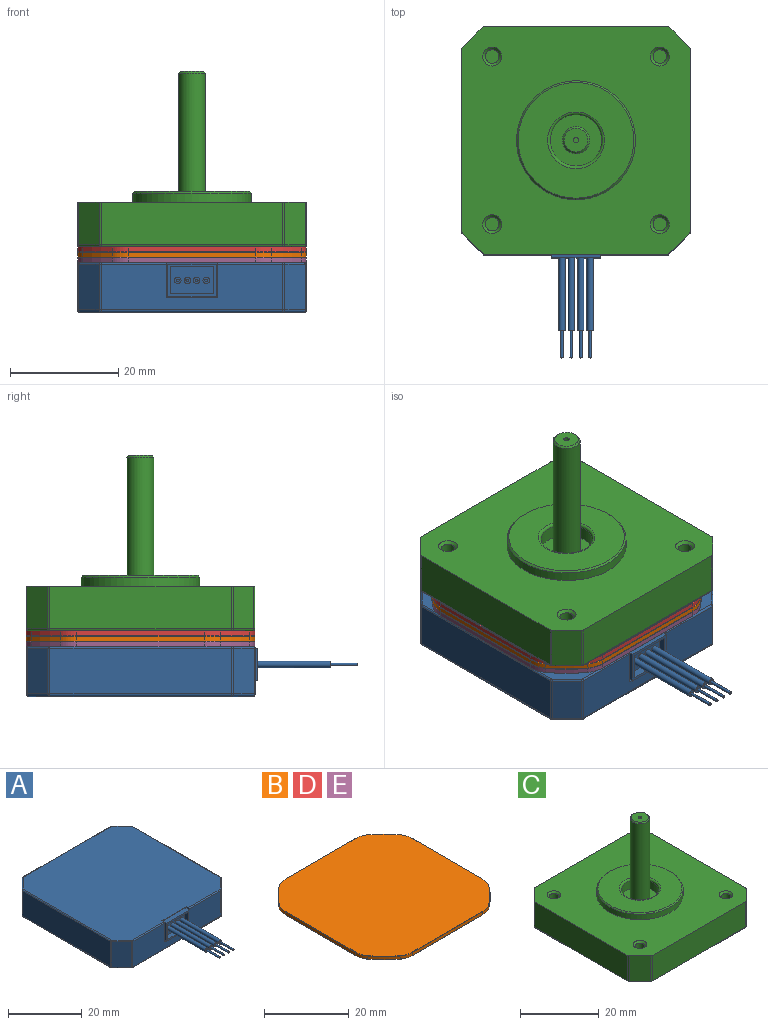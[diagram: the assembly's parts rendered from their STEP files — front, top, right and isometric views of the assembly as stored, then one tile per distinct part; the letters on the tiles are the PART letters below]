
ASSEMBLY  parts=5 mates=2
PART A: 89 faces, bbox 42.3x61.3x9.2 mm
  f0: plane 9.5x6.5mm, normal (0,-1,0), area 7.8mm2, adj f9,f43,f44,f45,f64,f65,f66,f67
  f1: plane 8.4x3.82mm, normal (-0.71,-0.71,0), area 45.4mm2, adj f30,f35,f36,f60
  f2: plane 33.65x8.4mm, normal (0,-1,0), area 223.8mm2, adj f36,f37,f41,f43,f44,f45,f46,f62
  f3: plane 8.4x3.82mm, normal (0.71,-0.71,0), area 45.4mm2, adj f31,f37,f38,f48
  f4: plane 33.65x8.4mm, normal (1,0,0), area 282.7mm2, adj f25,f31,f32,f50
  f5: plane 8.4x3.82mm, normal (0.71,0.71,0), area 45.4mm2, adj f19,f25,f26,f52
  f6: plane 33.65x8.4mm, normal (0,1,0), area 282.7mm2, adj f18,f19,f20,f54
  f7: plane 8.4x3.82mm, normal (-0.71,0.71,0), area 45.4mm2, adj f18,f23,f24,f56
  f8: plane 33.65x8.4mm, normal (-1,0,0), area 282.7mm2, adj f24,f29,f30,f58
  f9: plane 41.7x41.7mm, normal (0,0,1), area 1701.2mm2, adj f0,f43,f45,f46,f47,f48,f49,f50
  f10: plane 41.3x41.3mm, normal (0,0,-1), area 1589.9mm2, adj f20,f23,f26,f29,f32,f35,f38,f41
  f11: cylinder r=4.75mm len=9.5mm, axis (0,0,-1), area 89.5mm2, adj f12,f42
  f12: plane 9.5x9.5mm, normal (0,0,-1), area 51.2mm2, adj f11,f13
  f13: cylinder r=2.5mm len=5mm, axis (0,0,-1), area 3.1mm2, adj f12,f17
  f14: plane 4.4x4.4mm, normal (0,0,-1), area 14.4mm2, adj f15,f17
  f15: cylinder r=0.5mm len=1mm, axis (0,0,-1), area 1.6mm2, adj f14,f16
  f16: plane 1x1mm, normal (0,0,-1), area 0.8mm2, adj f15
  f17: cone r=2.2mm half-angle=45deg, axis (0,0,1), area 6.3mm2, adj f13,f14
  f18: cylinder r=0.5mm len=8.4mm, axis (0,0,-1), area 3.3mm2, adj f6,f7,f21,f55
  f19: cylinder r=0.5mm len=8.4mm, axis (0,0,-1), area 3.3mm2, adj f5,f6,f22,f53
  f20: cylinder r=0.5mm len=33.65mm, axis (-1,0,0), area 26.4mm2, adj f6,f10,f21,f22
  f21: sphere r=0.5mm, area 0.2mm2, adj f18,f20,f23
  f22: sphere r=0.5mm, area 0.2mm2, adj f19,f20,f26
  f23: cylinder r=0.5mm len=4.18mm, axis (-0.71,-0.71,0), area 4.2mm2, adj f7,f10,f21,f27
  f24: cylinder r=0.5mm len=8.4mm, axis (0,0,1), area 3.3mm2, adj f7,f8,f27,f57
  f25: cylinder r=0.5mm len=8.4mm, axis (0,0,-1), area 3.3mm2, adj f4,f5,f28,f51
  f26: cylinder r=0.5mm len=4.18mm, axis (-0.71,0.71,0), area 4.2mm2, adj f5,f10,f22,f28
  f27: sphere r=0.5mm, area 0.2mm2, adj f23,f24,f29
  f28: sphere r=0.5mm, area 0.2mm2, adj f25,f26,f32
  f29: cylinder r=0.5mm len=33.65mm, axis (0,-1,0), area 26.4mm2, adj f8,f10,f27,f33
  f30: cylinder r=0.5mm len=8.4mm, axis (0,0,1), area 3.3mm2, adj f1,f8,f33,f59
  f31: cylinder r=0.5mm len=8.4mm, axis (0,0,-1), area 3.3mm2, adj f3,f4,f34,f49
  f32: cylinder r=0.5mm len=33.65mm, axis (0,1,0), area 26.4mm2, adj f4,f10,f28,f34
  f33: sphere r=0.5mm, area 0.2mm2, adj f29,f30,f35
  f34: sphere r=0.5mm, area 0.2mm2, adj f31,f32,f38
  f35: cylinder r=0.5mm len=4.18mm, axis (0.71,-0.71,0), area 4.2mm2, adj f1,f10,f33,f39
  f36: cylinder r=0.5mm len=8.4mm, axis (0,0,1), area 3.3mm2, adj f1,f2,f39,f61
  f37: cylinder r=0.5mm len=8.4mm, axis (0,0,1), area 3.3mm2, adj f2,f3,f40,f47
  f38: cylinder r=0.5mm len=4.18mm, axis (0.71,0.71,0), area 4.2mm2, adj f3,f10,f34,f40
  f39: sphere r=0.5mm, area 0.2mm2, adj f35,f36,f41
  f40: sphere r=0.5mm, area 0.2mm2, adj f37,f38,f41
  f41: cylinder r=0.5mm len=33.65mm, axis (1,0,0), area 26.4mm2, adj f2,f10,f39,f40
  f42: torus R=5.25mm, axis (0,0,1), area 24.3mm2, adj f10,f11
  f43: plane 6.5x1mm, normal (-1,0,0), area 6.5mm2, adj f0,f2,f9,f44,f46
  f44: plane 9.5x1mm, normal (0,0,1), area 9.5mm2, adj f0,f2,f43,f45
  f45: plane 6.5x1mm, normal (1,0,0), area 6.5mm2, adj f0,f2,f9,f44,f62
  f46: cylinder r=0.3mm len=12.08mm, axis (-1,0,0), area 5.7mm2, adj f2,f9,f43,f47
  f47: torus R=0.2mm, axis (0,0,1), area 0.1mm2, adj f9,f37,f46,f48
  f48: cylinder r=0.3mm len=4.04mm, axis (-0.71,-0.71,0), area 2.5mm2, adj f3,f9,f47,f49
  f49: torus R=0.2mm, axis (0,0,1), area 0.1mm2, adj f9,f31,f48,f50
  f50: cylinder r=0.3mm len=33.65mm, axis (0,-1,0), area 15.9mm2, adj f4,f9,f49,f51
  f51: torus R=0.2mm, axis (0,0,1), area 0.1mm2, adj f9,f25,f50,f52
  f52: cylinder r=0.3mm len=4.04mm, axis (0.71,-0.71,0), area 2.5mm2, adj f5,f9,f51,f53
  f53: torus R=0.2mm, axis (0,0,1), area 0.1mm2, adj f9,f19,f52,f54
  f54: cylinder r=0.3mm len=33.65mm, axis (1,0,0), area 15.9mm2, adj f6,f9,f53,f55
  f55: torus R=0.2mm, axis (0,0,1), area 0.1mm2, adj f9,f18,f54,f56
  f56: cylinder r=0.3mm len=4.04mm, axis (0.71,0.71,0), area 2.5mm2, adj f7,f9,f55,f57
  f57: torus R=0.2mm, axis (0,0,1), area 0.1mm2, adj f9,f24,f56,f58
  f58: cylinder r=0.3mm len=33.65mm, axis (0,1,0), area 15.9mm2, adj f8,f9,f57,f59
  f59: torus R=0.2mm, axis (0,0,1), area 0.1mm2, adj f9,f30,f58,f60
  f60: cylinder r=0.3mm len=4.04mm, axis (-0.71,0.71,0), area 2.5mm2, adj f1,f9,f59,f61
  f61: torus R=0.2mm, axis (0,0,1), area 0.1mm2, adj f9,f36,f60,f62
  f62: cylinder r=0.3mm len=12.08mm, axis (-1,0,0), area 5.7mm2, adj f2,f9,f45,f61
  f63: plane 9x6mm, normal (0,-1,0), area 14mm2, adj f64,f65,f66,f67,f68,f69,f70,f71
  f64: plane 9x1.5mm, normal (0,0,-1), area 13.5mm2, adj f0,f63,f65,f67
  f65: plane 6x1.5mm, normal (1,0,0), area 9mm2, adj f0,f63,f64,f66
  f66: plane 9x1.5mm, normal (0,0,1), area 13.5mm2, adj f0,f63,f65,f67
  f67: plane 6x1.5mm, normal (-1,0,0), area 9mm2, adj f0,f63,f64,f66
  f68: plane 8x1.5mm, normal (0,0,1), area 12mm2, adj f63,f69,f71,f80
  f69: plane 5x1.5mm, normal (-1,0,0), area 7.5mm2, adj f63,f68,f70,f80
  f70: plane 8x1.5mm, normal (0,0,-1), area 12mm2, adj f63,f69,f71,f80
  f71: plane 5x1.5mm, normal (1,0,0), area 7.5mm2, adj f63,f68,f70,f80
  f72: plane 0.5x0.5mm, normal (0,-1,0), area 0.2mm2, adj f74
  f73: plane 0.5x0.5mm, normal (0,-1,0), area 0.2mm2, adj f75
  f74: cylinder r=0.25mm len=5mm, axis (0,1,0), area 7.9mm2, adj f72,f76
  f75: cylinder r=0.25mm len=5mm, axis (0,1,0), area 7.9mm2, adj f73,f77
  f76: plane 1.2x1.2mm, normal (0,-1,0), area 0.9mm2, adj f74,f78
  f77: plane 1.2x1.2mm, normal (0,-1,0), area 0.9mm2, adj f75,f79
  f78: cylinder r=0.6mm len=15mm, axis (0,1,0), area 56.5mm2, adj f76,f80
  f79: cylinder r=0.6mm len=15mm, axis (0,1,0), area 56.5mm2, adj f77,f80
  f80: plane 8x5mm, normal (0,-1,0), area 35.5mm2, adj f68,f69,f70,f71,f78,f79,f82,f86
  f81: plane 1.2x1.2mm, normal (0,-1,0), area 0.9mm2, adj f82,f83
  f82: cylinder r=0.6mm len=15mm, axis (0,1,0), area 56.5mm2, adj f80,f81
  f83: cylinder r=0.25mm len=5mm, axis (0,1,0), area 7.9mm2, adj f81,f84
  f84: plane 0.5x0.5mm, normal (0,-1,0), area 0.2mm2, adj f83
  f85: plane 1.2x1.2mm, normal (0,-1,0), area 0.9mm2, adj f86,f87
  f86: cylinder r=0.6mm len=15mm, axis (0,1,0), area 56.5mm2, adj f80,f85
  f87: cylinder r=0.25mm len=5mm, axis (0,1,0), area 7.9mm2, adj f85,f88
  f88: plane 0.5x0.5mm, normal (0,-1,0), area 0.2mm2, adj f87
PART B: 50 faces, bbox 42.3x42.3x1 mm
  f0: cylinder r=5mm len=2.95mm, axis (0,0,-1), area 2.8mm2, adj f1,f15,f27,f43
  f1: plane 23.59x0.9mm, normal (0,1,0), area 21.2mm2, adj f0,f2,f29,f45
  f2: cylinder r=5mm len=2.95mm, axis (0,0,-1), area 2.8mm2, adj f1,f3,f31,f47
  f3: cylinder r=25mm len=5.44mm, axis (0,0,-1), area 7mm2, adj f2,f4,f33,f49
  f4: cylinder r=5mm len=2.95mm, axis (0,0,-1), area 2.8mm2, adj f3,f5,f32,f48
  f5: plane 23.59x0.9mm, normal (-1,0,0), area 21.2mm2, adj f4,f6,f30,f46
  f6: cylinder r=5mm len=2.95mm, axis (0,0,-1), area 2.8mm2, adj f5,f7,f28,f44
  f7: cylinder r=25mm len=5.44mm, axis (0,0,-1), area 7mm2, adj f6,f8,f26,f42
  f8: cylinder r=5mm len=2.95mm, axis (0,0,-1), area 2.8mm2, adj f7,f9,f24,f40
  f9: plane 23.59x0.9mm, normal (0,-1,0), area 21.2mm2, adj f8,f10,f22,f38
  f10: cylinder r=5mm len=2.95mm, axis (0,0,-1), area 2.8mm2, adj f9,f11,f20,f36
  f11: cylinder r=25mm len=5.44mm, axis (0,0,-1), area 7mm2, adj f10,f12,f18,f34
  f12: cylinder r=5mm len=2.95mm, axis (0,0,-1), area 2.8mm2, adj f11,f13,f19,f35
  f13: plane 23.59x0.9mm, normal (1,0,0), area 21.2mm2, adj f12,f14,f21,f37
  f14: cylinder r=5mm len=2.95mm, axis (0,0,-1), area 2.8mm2, adj f13,f15,f23,f39
  f15: cylinder r=25mm len=5.44mm, axis (0,0,-1), area 7mm2, adj f0,f14,f25,f41
  f16: plane 42.2x42.2mm, normal (0,0,1), area 1675.8mm2, adj f18,f19,f20,f21,f22,f23,f24,f25
  f17: plane 42.2x42.2mm, normal (0,0,-1), area 1675.8mm2, adj f34,f35,f36,f37,f38,f39,f40,f41
  f18: cone r=24.95mm half-angle=45deg, axis (0,0,-1), area 0.5mm2, adj f11,f16,f19,f20
  f19: cone r=4.95mm half-angle=45deg, axis (0,0,-1), area 0.2mm2, adj f12,f16,f18,f21
  f20: cone r=4.95mm half-angle=45deg, axis (0,0,-1), area 0.2mm2, adj f10,f16,f18,f22
  f21: plane 23.59x0.05mm, normal (0.71,0,0.71), area 1.7mm2, adj f13,f16,f19,f23
  f22: plane 23.59x0.05mm, normal (0,-0.71,0.71), area 1.7mm2, adj f9,f16,f20,f24
  f23: cone r=4.95mm half-angle=45deg, axis (0,0,-1), area 0.2mm2, adj f14,f16,f21,f25
  f24: cone r=4.95mm half-angle=45deg, axis (0,0,-1), area 0.2mm2, adj f8,f16,f22,f26
  f25: cone r=24.95mm half-angle=45deg, axis (0,0,-1), area 0.5mm2, adj f15,f16,f23,f27
  f26: cone r=24.95mm half-angle=45deg, axis (0,0,-1), area 0.5mm2, adj f7,f16,f24,f28
  f27: cone r=4.95mm half-angle=45deg, axis (0,0,-1), area 0.2mm2, adj f0,f16,f25,f29
  f28: cone r=4.95mm half-angle=45deg, axis (0,0,-1), area 0.2mm2, adj f6,f16,f26,f30
  f29: plane 23.59x0.05mm, normal (0,0.71,0.71), area 1.7mm2, adj f1,f16,f27,f31
  f30: plane 23.59x0.05mm, normal (-0.71,0,0.71), area 1.7mm2, adj f5,f16,f28,f32
  f31: cone r=4.95mm half-angle=45deg, axis (0,0,-1), area 0.2mm2, adj f2,f16,f29,f33
  f32: cone r=4.95mm half-angle=45deg, axis (0,0,-1), area 0.2mm2, adj f4,f16,f30,f33
  f33: cone r=24.95mm half-angle=45deg, axis (0,0,-1), area 0.5mm2, adj f3,f16,f31,f32
  f34: cone r=25mm half-angle=45deg, axis (0,0,1), area 0.5mm2, adj f11,f17,f35,f36
  f35: cone r=5mm half-angle=45deg, axis (0,0,1), area 0.2mm2, adj f12,f17,f34,f37
  f36: cone r=5mm half-angle=45deg, axis (0,0,1), area 0.2mm2, adj f10,f17,f34,f38
  f37: plane 23.59x0.05mm, normal (0.71,0,-0.71), area 1.7mm2, adj f13,f17,f35,f39
  f38: plane 23.59x0.05mm, normal (0,-0.71,-0.71), area 1.7mm2, adj f9,f17,f36,f40
  f39: cone r=5mm half-angle=45deg, axis (0,0,1), area 0.2mm2, adj f14,f17,f37,f41
  f40: cone r=5mm half-angle=45deg, axis (0,0,1), area 0.2mm2, adj f8,f17,f38,f42
  f41: cone r=25mm half-angle=45deg, axis (0,0,1), area 0.5mm2, adj f15,f17,f39,f43
  f42: cone r=25mm half-angle=45deg, axis (0,0,1), area 0.5mm2, adj f7,f17,f40,f44
  f43: cone r=5mm half-angle=45deg, axis (0,0,1), area 0.2mm2, adj f0,f17,f41,f45
  f44: cone r=5mm half-angle=45deg, axis (0,0,1), area 0.2mm2, adj f6,f17,f42,f46
  f45: plane 23.59x0.05mm, normal (0,0.71,-0.71), area 1.7mm2, adj f1,f17,f43,f47
  f46: plane 23.59x0.05mm, normal (-0.71,0,-0.71), area 1.7mm2, adj f5,f17,f44,f48
  f47: cone r=5mm half-angle=45deg, axis (0,0,1), area 0.2mm2, adj f2,f17,f45,f49
  f48: cone r=5mm half-angle=45deg, axis (0,0,1), area 0.2mm2, adj f4,f17,f46,f49
  f49: cone r=25mm half-angle=45deg, axis (0,0,1), area 0.5mm2, adj f3,f17,f47,f48
PART C: 57 faces, bbox 42.3x42.3x32.4 mm
  f0: plane 7.9x3.82mm, normal (-0.71,-0.71,0), area 42.7mm2, adj f9,f12,f13,f47
  f1: plane 33.65x7.9mm, normal (-1,0,0), area 265.9mm2, adj f9,f13,f14,f43
  f2: plane 7.9x3.82mm, normal (-0.71,0.71,0), area 42.7mm2, adj f9,f14,f15,f42
  f3: plane 33.65x7.9mm, normal (0,1,0), area 265.9mm2, adj f9,f15,f16,f46
  f4: plane 7.9x3.82mm, normal (0.71,0.71,0), area 42.7mm2, adj f9,f16,f17,f50
  f5: plane 33.65x7.9mm, normal (1,0,0), area 265.9mm2, adj f9,f10,f17,f54
  f6: plane 7.9x3.82mm, normal (0.71,-0.71,0), area 42.7mm2, adj f9,f10,f11,f55
  f7: plane 33.65x7.9mm, normal (0,-1,0), area 265.9mm2, adj f9,f11,f12,f51
  f8: plane 41.7x41.7mm, normal (0,0,-1), area 1707.8mm2, adj f41,f42,f43,f44,f45,f46,f47,f48
  f9: plane 42.3x42.3mm, normal (0,0,1), area 1336.7mm2, adj f0,f1,f2,f3,f4,f5,f6,f7
  f10: cylinder r=0.5mm len=7.9mm, axis (0,0,1), area 3.1mm2, adj f5,f6,f9,f56
  f11: cylinder r=0.5mm len=7.9mm, axis (0,0,-1), area 3.1mm2, adj f6,f7,f9,f53
  f12: cylinder r=0.5mm len=7.9mm, axis (0,0,-1), area 3.1mm2, adj f0,f7,f9,f49
  f13: cylinder r=0.5mm len=7.9mm, axis (0,0,-1), area 3.1mm2, adj f0,f1,f9,f45
  f14: cylinder r=0.5mm len=7.9mm, axis (0,0,-1), area 3.1mm2, adj f1,f2,f9,f41
  f15: cylinder r=0.5mm len=7.9mm, axis (0,0,1), area 3.1mm2, adj f2,f3,f9,f44
  f16: cylinder r=0.5mm len=7.9mm, axis (0,0,1), area 3.1mm2, adj f3,f4,f9,f48
  f17: cylinder r=0.5mm len=7.9mm, axis (0,0,1), area 3.1mm2, adj f4,f5,f9,f52
  f18: plane 21.4x21.4mm, normal (0,0,1), area 273.1mm2, adj f22,f23
  f19: cylinder r=11mm len=22mm, axis (0,0,-1), area 117.5mm2, adj f9,f22
  f20: cylinder r=4.75mm len=9.5mm, axis (0,0,-1), area 74.6mm2, adj f21,f23
  f21: plane 9.5x9.5mm, normal (0,0,1), area 51.2mm2, adj f20,f24
  f22: cone r=10.7mm half-angle=45deg, axis (0,0,-1), area 28.9mm2, adj f18,f19
  f23: torus R=5.25mm, axis (0,0,1), area 24.3mm2, adj f18,f20
  f24: cylinder r=2.5mm len=24.9mm, axis (0,0,-1), area 391.1mm2, adj f21,f26
  f25: plane 4.4x4.4mm, normal (0,0,1), area 14.4mm2, adj f26,f27
  f26: cone r=2.2mm half-angle=45deg, axis (0,0,-1), area 6.3mm2, adj f24,f25
  f27: cylinder r=0.5mm len=1mm, axis (0,0,1), area 3.1mm2, adj f25,f28
  f28: plane 1x1mm, normal (0,0,1), area 0.8mm2, adj f27
  f29: cylinder r=1.25mm len=6.5mm, axis (0,0,1), area 51.1mm2, adj f30,f40
  f30: plane 2.5x2.5mm, normal (0,0,1), area 4.9mm2, adj f29
  f31: cylinder r=1.25mm len=6.5mm, axis (0,0,1), area 51.1mm2, adj f32,f37
  f32: plane 2.5x2.5mm, normal (0,0,1), area 4.9mm2, adj f31
  f33: cylinder r=1.25mm len=6.5mm, axis (0,0,1), area 51.1mm2, adj f34,f38
  f34: plane 2.5x2.5mm, normal (0,0,1), area 4.9mm2, adj f33
  f35: cylinder r=1.25mm len=6.5mm, axis (0,0,1), area 51.1mm2, adj f36,f39
  f36: plane 2.5x2.5mm, normal (0,0,1), area 4.9mm2, adj f35
  f37: cone r=1.25mm half-angle=45deg, axis (0,0,1), area 6.7mm2, adj f9,f31
  f38: cone r=1.25mm half-angle=45deg, axis (0,0,1), area 6.7mm2, adj f9,f33
  f39: cone r=1.25mm half-angle=45deg, axis (0,0,1), area 6.7mm2, adj f9,f35
  f40: cone r=1.25mm half-angle=45deg, axis (0,0,1), area 6.7mm2, adj f9,f29
  f41: torus R=0.2mm, axis (0,0,1), area 0.1mm2, adj f8,f14,f42,f43
  f42: cylinder r=0.3mm len=4.04mm, axis (0.71,0.71,0), area 2.5mm2, adj f2,f8,f41,f44
  f43: cylinder r=0.3mm len=33.65mm, axis (0,1,0), area 15.9mm2, adj f1,f8,f41,f45
  f44: torus R=0.2mm, axis (0,0,1), area 0.1mm2, adj f8,f15,f42,f46
  f45: torus R=0.2mm, axis (0,0,1), area 0.1mm2, adj f8,f13,f43,f47
  f46: cylinder r=0.3mm len=33.65mm, axis (1,0,0), area 15.9mm2, adj f3,f8,f44,f48
  f47: cylinder r=0.3mm len=4.04mm, axis (-0.71,0.71,0), area 2.5mm2, adj f0,f8,f45,f49
  f48: torus R=0.2mm, axis (0,0,1), area 0.1mm2, adj f8,f16,f46,f50
  f49: torus R=0.2mm, axis (0,0,1), area 0.1mm2, adj f8,f12,f47,f51
  f50: cylinder r=0.3mm len=4.04mm, axis (0.71,-0.71,0), area 2.5mm2, adj f4,f8,f48,f52
  f51: cylinder r=0.3mm len=33.65mm, axis (-1,0,0), area 15.9mm2, adj f7,f8,f49,f53
  f52: torus R=0.2mm, axis (0,0,1), area 0.1mm2, adj f8,f17,f50,f54
  f53: torus R=0.2mm, axis (0,0,1), area 0.1mm2, adj f8,f11,f51,f55
  f54: cylinder r=0.3mm len=33.65mm, axis (0,-1,0), area 15.9mm2, adj f5,f8,f52,f56
  f55: cylinder r=0.3mm len=4.04mm, axis (-0.71,-0.71,0), area 2.5mm2, adj f6,f8,f53,f56
  f56: torus R=0.2mm, axis (0,0,1), area 0.1mm2, adj f8,f10,f54,f55
PART D: same geometry as B
PART E: same geometry as B
PLACE A t=(0,-0.08,-20.4)mm
PLACE B t=(0,0,-19.4)mm
PLACE C t=(0,0,-59.4)mm
PLACE D t=(0,0,-18.4)mm
PLACE E t=(0,0,-20.4)mm
MATE fastened A.f9 <-> C.f19  axis (0,0,1) through (0,0,-11.2)mm
MATE fastened D.f3 <-> C.f19  axis (0,0,1) through (0,0,-8.2)mm
